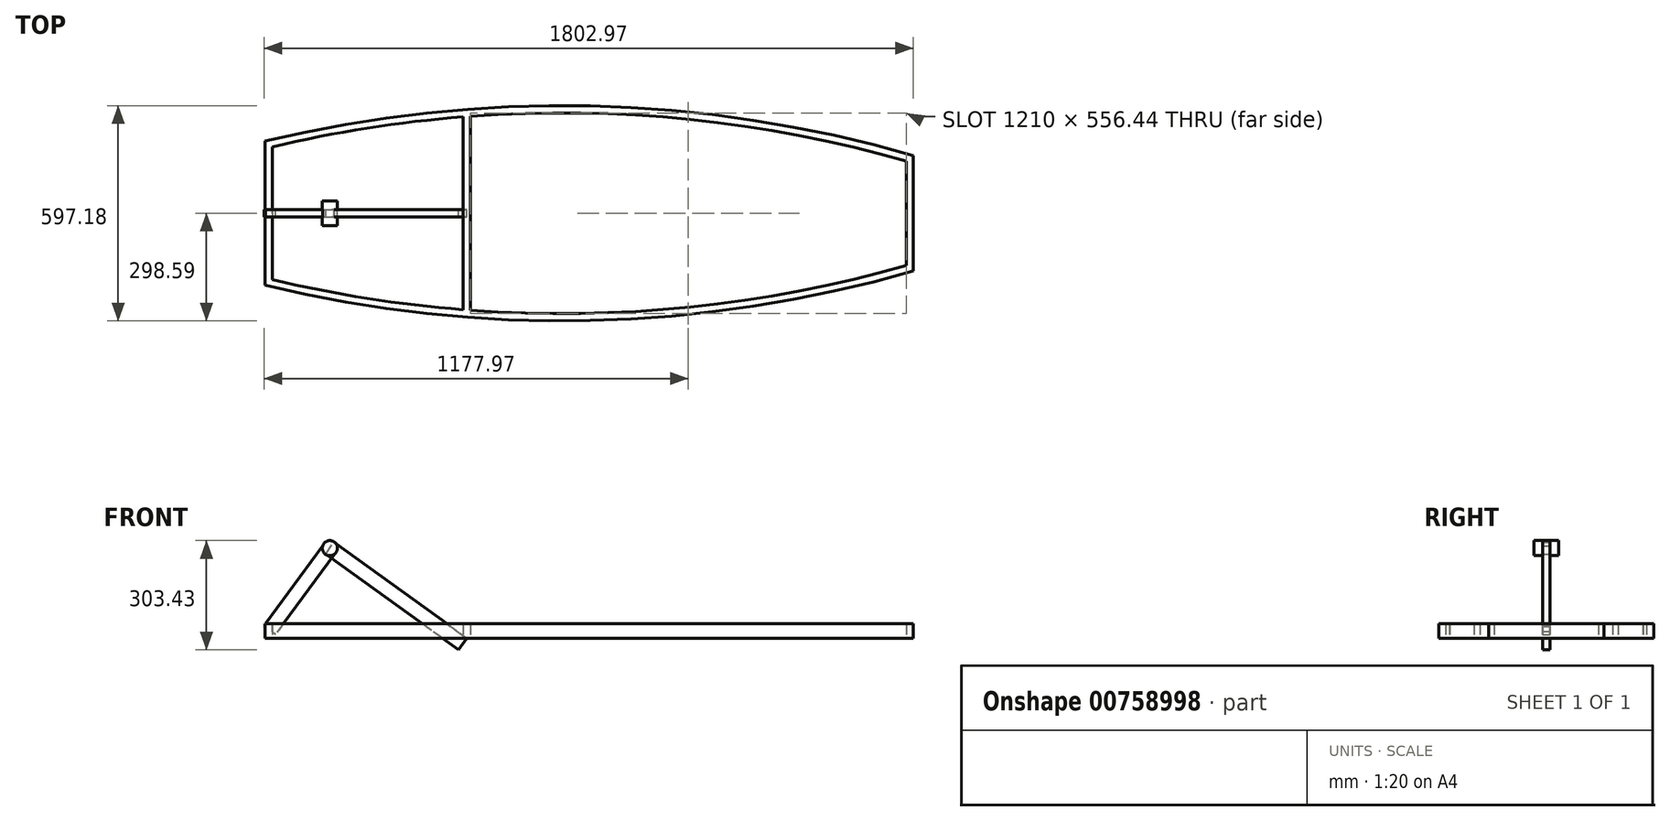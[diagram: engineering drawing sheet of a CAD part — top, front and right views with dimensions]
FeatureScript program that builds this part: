
annotation { "Feature Type Name" : "Feature", "Feature Type Description" : "" }
export const myFeature = defineFeature(function(context is Context, id is Id, definition is map)
    precondition{}
    {
        {
            var Q0;
            Q0=qCreatedBy(makeId("Top.planeOp"),FACE);
            var sketch = newSketch(context, id + "F0", { "sketchPlane" : qUnion([Q0])});
            skLineSegment(sketch, "E0", {"start": v(0, 0) * mm, "end": v(1800, 0) * mm, "construction": true});
            skArc(sketch, "E1", {"start": v(1800, 160) * mm, "mid": v(902.62, 297.72) * mm, "end": v(0, 200) * mm});
            skLineSegment(sketch, "E2", {"start": v(0, 0) * mm, "end": v(0, 200) * mm});
            skLineSegment(sketch, "E3", {"start": v(1800, 0) * mm, "end": v(1800, 160) * mm});
            skArc(sketch, "E4.0", {"start": v(1780, 144.94) * mm, "mid": v(1180.47, 260.37) * mm, "end": v(570, 269.24) * mm});
            skLineSegment(sketch, "E5.0", {"start": v(20, 0) * mm, "end": v(20, 184.23) * mm});
            skLineSegment(sketch, "E6.0", {"start": v(1780, 0) * mm, "end": v(1780, 144.94) * mm});
            skLineSegment(sketch, "E7", {"start": v(0, 0) * mm, "end": v(20, 0) * mm});
            skLineSegment(sketch, "E8", {"start": v(1780, 0) * mm, "end": v(1800, 0) * mm});
            skLineSegment(sketch, "E9", {"start": v(550, 0) * mm, "end": v(570, 0) * mm});
            skLineSegment(sketch, "E10", {"start": v(570, 0) * mm, "end": v(570, 269.24) * mm});
            skLineSegment(sketch, "E11", {"start": v(550, 0) * mm, "end": v(550, 267.72) * mm});
            skArc(sketch, "E12.trimOffspring", {"start": v(550, 267.72) * mm, "mid": v(283.39, 236.2) * mm, "end": v(20, 184.23) * mm});
            skSolve(sketch);
        }
        {
            var Q0;
            Q0=makeQuery(id+"F0.imprint","IMPRINT",FACE,{"disambiguationData":[TD([[makeQuery(id+"F0.imprint","IMPRINT",EDGE,{"derivedFrom":sQuery(id+"F0.wireOp",EDGE,"E1")}),1.0]])]});
            extrude(context, id + "F1", {"entities" : qUnion([Q0]), "depth" : 40 * mm, "offsetDistance" : 25 * mm});
        }
        {
            var Q0;
            Q0=makeQuery(id+"F1.opExtrude","SWEPT_BODY",BODY,{"disambiguationData":[OSD([sQuery(id+"F0.wireOp",EDGE,"E1"),sQuery(id+"F0.wireOp",EDGE,"E2"),sQuery(id+"F0.wireOp",EDGE,"E3"),sQuery(id+"F0.wireOp",EDGE,"E4.0"),sQuery(id+"F0.wireOp",EDGE,"E5.0"),sQuery(id+"F0.wireOp",EDGE,"E6.0"),sQuery(id+"F0.wireOp",EDGE,"E7"),sQuery(id+"F0.wireOp",EDGE,"E8")])]});
            var Q1;
            Q1=qCreatedBy(makeId("Front.planeOp"),FACE);
            mirror(context, id + "F2", {"operationType" : NewBodyOperationType.ADD, "entities" : qUnion([Q0]), "mirrorPlane" : qUnion([Q1])});
        }
        {
            var Q0;
            Q0=qCreatedBy(makeId("Front.planeOp"),FACE);
            var sketch = newSketch(context, id + "F3", { "sketchPlane" : qUnion([Q0])});
            skLineSegment(sketch, "E13", {"start": v(20, 0) * mm, "end": v(180, 180) * mm, "construction": true});
            skLineSegment(sketch, "E14", {"start": v(180, 225.16) * mm, "end": v(0, 22.66) * mm, "construction": true});
            skLineSegment(sketch, "E15", {"start": v(0, 22.66) * mm, "end": v(20, 0) * mm, "construction": true});
            skCircle(sketch, "E16", {"center": v(180, 250) * mm, "radius": 21 * mm});
            skCircle(sketch, "E17", {"center": v(180, 250) * mm, "radius": 170 * mm, "construction": true});
            skCircle(sketch, "E18", {"center": v(139.65, 352.33) * mm, "radius": 170 * mm, "construction": true});
            skCircle(sketch, "E19", {"center": v(253.37, 63.94) * mm, "radius": 170 * mm, "construction": true});
            skLineSegment(sketch, "E20", {"start": v(139.65, 352.33) * mm, "end": v(253.37, 63.94) * mm, "construction": true});
            skLineSegment(sketch, "E21", {"start": v(180, 225.16) * mm, "end": v(180, 180) * mm, "construction": true});
            skSolve(sketch);
        }
        {
            var Q0;
            Q0=makeQuery(id+"F3.imprint","IMPRINT",FACE,{"disambiguationData":[TD([[makeQuery(id+"F3.imprint","IMPRINT",EDGE,{"derivedFrom":sQuery(id+"F3.wireOp",EDGE,"E16")}),1.0]])]});
            extrude(context, id + "F4", {"entities" : qUnion([Q0]), "operationType" : NewBodyOperationType.ADD, "endBound" : BoundingType.SYMMETRIC, "depth" : 68 * mm, "offsetDistance" : 25 * mm});
        }
        {
            var Q0;
            Q0=qCreatedBy(makeId("Front.planeOp"),FACE);
            var sketch = newSketch(context, id + "F5", { "sketchPlane" : qUnion([Q0])});
            skLineSegment(sketch, "E22", {"start": v(163.86, 261.82) * mm, "end": v(196.14, 238.18) * mm});
            skLineSegment(sketch, "E23", {"start": v(196.14, 238.18) * mm, "end": v(29.3, 10.37) * mm});
            skLineSegment(sketch, "E24", {"start": v(29.3, 10.37) * mm, "end": v(-2.97, 34) * mm});
            skLineSegment(sketch, "E25", {"start": v(-2.97, 34) * mm, "end": v(163.86, 261.82) * mm});
            skPoint(sketch, "E26.endSnap0", {"position": v(180, 250) * mm});
            skSolve(sketch);
        }
        {
            var Q0;
            Q0 = qSketchRegion(id + "F5", true);
            extrude(context, id + "F6", {"entities" : qUnion([Q0]), "operationType" : NewBodyOperationType.ADD, "endBound" : BoundingType.SYMMETRIC, "depth" : 20 * mm, "offsetDistance" : 25 * mm});
        }
        {
            var Q0;
            Q0=qCreatedBy(makeId("Front.planeOp"),FACE);
            var sketch = newSketch(context, id + "F7", { "sketchPlane" : qUnion([Q0])});
            skLineSegment(sketch, "E27", {"start": v(191.7, 266.22) * mm, "end": v(560.5, 0) * mm});
            skLineSegment(sketch, "E28", {"start": v(560.5, 0) * mm, "end": v(537.08, -32.43) * mm});
            skLineSegment(sketch, "E29", {"start": v(537.08, -32.43) * mm, "end": v(168.3, 233.78) * mm});
            skLineSegment(sketch, "E30", {"start": v(168.3, 233.78) * mm, "end": v(191.7, 266.22) * mm});
            skLineSegment(sketch, "E31", {"start": v(180, 250) * mm, "end": v(548.79, -16.22) * mm});
            skSolve(sketch);
        }
        {
            var Q0;
            Q0 = qSketchRegion(id + "F7", true);
            extrude(context, id + "F8", {"entities" : qUnion([Q0]), "endBound" : BoundingType.SYMMETRIC, "depth" : 20 * mm, "offsetDistance" : 25 * mm});
        }
    });
